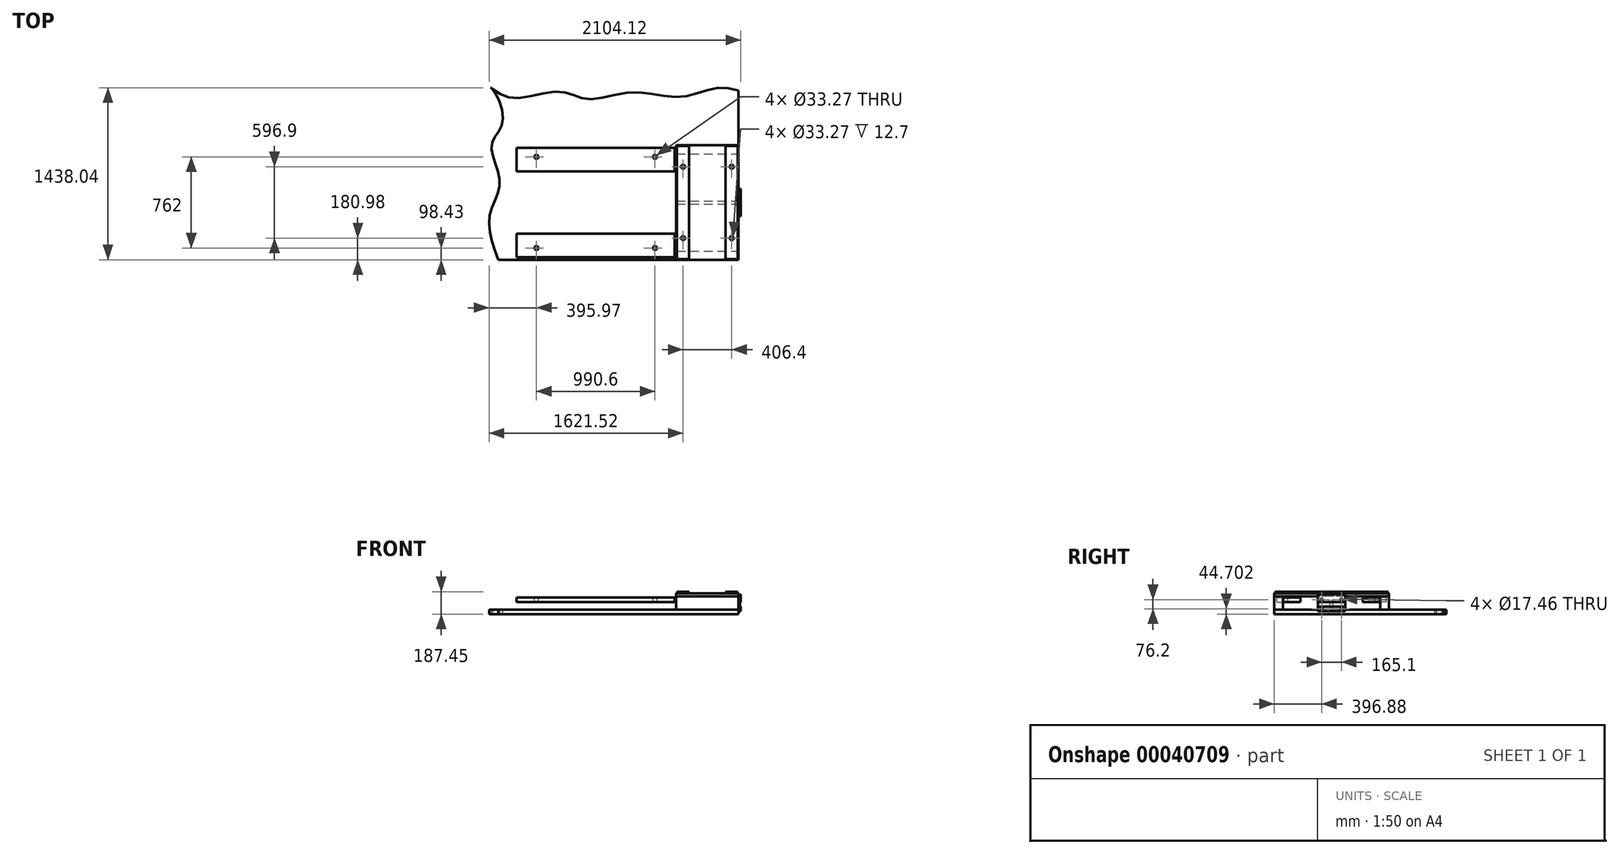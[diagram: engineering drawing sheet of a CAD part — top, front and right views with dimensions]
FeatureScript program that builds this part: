
annotation { "Feature Type Name" : "Feature", "Feature Type Description" : "" }
export const myFeature = defineFeature(function(context is Context, id is Id, definition is map)
    precondition{}
    {
        {
            var Q0;
            Q0=qCreatedBy(makeId("Top.planeOp"),FACE);
            var sketch = newSketch(context, id + "F0", { "sketchPlane" : qUnion([Q0])});
            skLineSegment(sketch, "E0.rect.bottom", {"start": v(-260.35, 479.43) * mm, "end": v(260.35, 479.43) * mm});
            skLineSegment(sketch, "E0.rect.top", {"start": v(-260.35, -479.43) * mm, "end": v(260.35, -479.43) * mm});
            skLineSegment(sketch, "E0.rect.left", {"start": v(-260.35, 479.43) * mm, "end": v(-260.35, -479.43) * mm});
            skLineSegment(sketch, "E0.rect.right", {"start": v(260.35, 479.43) * mm, "end": v(260.35, -479.43) * mm});
            skPoint(sketch, "E0.rect.middle", {"position": v(0, 0) * mm});
            skSolve(sketch);
        }
        {
            var Q0;
            Q0 = qSketchRegion(id + "F0", true);
            extrude(context, id + "F1", {"entities" : qUnion([Q0]), "oppositeDirection" : true, "depth" : 25.4 * mm});
        }
        {
            var Q0;
            Q0=makeQuery(id+"F1.opExtrude","CAP_FACE",FACE,{"disambiguationData":[OSD([sQuery(id+"F0.wireOp",EDGE,"E0.rect.bottom"),sQuery(id+"F0.wireOp",EDGE,"E0.rect.top"),sQuery(id+"F0.wireOp",EDGE,"E0.rect.left"),sQuery(id+"F0.wireOp",EDGE,"E0.rect.right")])],"isStart":true});
            var sketch = newSketch(context, id + "F2", { "sketchPlane" : qUnion([Q0])});
            skLineSegment(sketch, "E1", {"start": v(0, 479.43) * mm, "end": v(0, -479.43) * mm, "construction": true});
            skLineSegment(sketch, "E2.0", {"start": v(152.4, 479.43) * mm, "end": v(152.4, -479.43) * mm, "construction": true});
            skLineSegment(sketch, "E3.0", {"start": v(254, 479.43) * mm, "end": v(254, -479.43) * mm, "construction": true});
            skLineSegment(sketch, "E4.0", {"start": v(-260.35, 479.43) * mm, "end": v(260.35, 479.43) * mm, "construction": true});
            skLineSegment(sketch, "E5.0", {"start": v(-260.35, 473.08) * mm, "end": v(260.35, 473.08) * mm, "construction": true});
            skLineSegment(sketch, "E6.bottom", {"start": v(152.4, 473.08) * mm, "end": v(254, 473.08) * mm});
            skLineSegment(sketch, "E6.top", {"start": v(152.4, -473.07) * mm, "end": v(254, -473.07) * mm});
            skLineSegment(sketch, "E6.left", {"start": v(152.4, 473.08) * mm, "end": v(152.4, -473.07) * mm});
            skLineSegment(sketch, "E6.right", {"start": v(254, 473.08) * mm, "end": v(254, -473.07) * mm});
            skLineSegment(sketch, "E7.0", {"start": v(203.2, 479.43) * mm, "end": v(203.2, -479.43) * mm, "construction": true});
            skLineSegment(sketch, "E8", {"start": v(-359.3, 0) * mm, "end": v(385.16, 0) * mm, "construction": true});
            skLineSegment(sketch, "E9.0", {"start": v(-359.3, 298.45) * mm, "end": v(385.16, 298.45) * mm, "construction": true});
            skCircle(sketch, "E10", {"center": v(203.2, 298.45) * mm, "radius": 16.64 * mm});
            skCircle(sketch, "E11.MirrorC", {"center": v(203.2, -298.45) * mm, "radius": 16.64 * mm});
            skLineSegment(sketch, "E12.MirrorCS", {"start": v(-254, 479.43) * mm, "end": v(-254, -479.42) * mm});
            skLineSegment(sketch, "E13.MirrorCS", {"start": v(-152.4, 479.43) * mm, "end": v(-152.4, -479.42) * mm});
            skLineSegment(sketch, "E14.MirrorCS", {"start": v(-152.4, -473.07) * mm, "end": v(-254, -473.07) * mm});
            skLineSegment(sketch, "E15.MirrorCS", {"start": v(-152.4, 473.08) * mm, "end": v(-152.4, -473.07) * mm});
            skLineSegment(sketch, "E16.MirrorCS", {"start": v(-254, 473.08) * mm, "end": v(-254, -473.07) * mm});
            skLineSegment(sketch, "E17.MirrorCS", {"start": v(-152.4, 473.08) * mm, "end": v(-254, 473.08) * mm});
            skCircle(sketch, "E18.MirrorC", {"center": v(-203.2, -298.45) * mm, "radius": 16.64 * mm});
            skLineSegment(sketch, "E19.MirrorCS", {"start": v(-203.2, 479.43) * mm, "end": v(-203.2, -479.43) * mm, "construction": true});
            skCircle(sketch, "E20.MirrorC", {"center": v(-203.2, 298.45) * mm, "radius": 16.64 * mm});
            skSolve(sketch);
        }
        {
            var Q0;
            Q0 = qSketchRegion(id + "F2", true);
            extrude(context, id + "F3", {"entities" : qUnion([Q0]), "operationType" : NewBodyOperationType.ADD, "depth" : 12.7 * mm});
        }
        {
            var Q0;
            Q0=makeQuery(id+"F3.opExtrude","CAP_FACE",FACE,{"disambiguationData":[OSD([sQuery(id+"F2.wireOp",EDGE,"E14.MirrorCS"),sQuery(id+"F2.wireOp",EDGE,"E15.MirrorCS"),sQuery(id+"F2.wireOp",EDGE,"E16.MirrorCS"),sQuery(id+"F2.wireOp",EDGE,"E17.MirrorCS"),sQuery(id+"F2.wireOp",EDGE,"E18.MirrorC"),sQuery(id+"F2.wireOp",EDGE,"E20.MirrorC")])],"isStart":false});
            cPlane(context, id + "F4", {"entities" : qUnion([Q0]), "cplaneType" : CPlaneType.OFFSET, "offset" : 47.75 * mm, "oppositeDirection" : true, "width" : 152.4 * mm, "height" : 152.4 * mm});
        }
        {
            var Q0;
            Q0=qCreatedBy(id+"F4.planeOp",FACE);
            var sketch = newSketch(context, id + "F5", { "sketchPlane" : qUnion([Q0])});
            skLineSegment(sketch, "E21", {"start": v(0, 742.56) * mm, "end": v(0, -827.84) * mm, "construction": true});
            skLineSegment(sketch, "E22", {"start": v(458.96, 0) * mm, "end": v(-1901, 0) * mm, "construction": true});
            skLineSegment(sketch, "E23.0", {"start": v(-933.45, 742.56) * mm, "end": v(-933.45, -827.84) * mm, "construction": true});
            skLineSegment(sketch, "E24.0", {"start": v(-273.05, 742.56) * mm, "end": v(-273.05, -827.84) * mm, "construction": true});
            skLineSegment(sketch, "E25.0", {"start": v(-1593.85, 742.56) * mm, "end": v(-1593.85, -827.84) * mm, "construction": true});
            skLineSegment(sketch, "E26.0", {"start": v(458.96, -381) * mm, "end": v(-1901, -381) * mm, "construction": true});
            skLineSegment(sketch, "E27.0", {"start": v(458.96, -457.2) * mm, "end": v(-1901, -457.2) * mm, "construction": true});
            skLineSegment(sketch, "E28.0", {"start": v(458.96, -260.35) * mm, "end": v(-1901, -260.35) * mm, "construction": true});
            skLineSegment(sketch, "E29.bottom", {"start": v(-273.05, -457.2) * mm, "end": v(-1593.85, -457.2) * mm});
            skLineSegment(sketch, "E29.top", {"start": v(-273.05, -260.35) * mm, "end": v(-1593.85, -260.35) * mm});
            skLineSegment(sketch, "E29.left", {"start": v(-273.05, -457.2) * mm, "end": v(-273.05, -260.35) * mm});
            skLineSegment(sketch, "E29.right", {"start": v(-1593.85, -457.2) * mm, "end": v(-1593.85, -260.35) * mm});
            skLineSegment(sketch, "E30.0", {"start": v(-1428.75, 742.56) * mm, "end": v(-1428.75, -827.84) * mm, "construction": true});
            skCircle(sketch, "E31", {"center": v(-1428.75, -381) * mm, "radius": 16.64 * mm});
            skCircle(sketch, "E32.MirrorC", {"center": v(-438.15, -381) * mm, "radius": 16.64 * mm});
            skCircle(sketch, "E33.MirrorC", {"center": v(-438.15, 381) * mm, "radius": 16.64 * mm});
            skCircle(sketch, "E34.MirrorC", {"center": v(-1428.75, 381) * mm, "radius": 16.64 * mm});
            skLineSegment(sketch, "E35.MirrorCS", {"start": v(-273.05, 457.2) * mm, "end": v(-273.05, 260.35) * mm});
            skLineSegment(sketch, "E36.MirrorCS", {"start": v(-273.05, 260.35) * mm, "end": v(-1593.85, 260.35) * mm});
            skLineSegment(sketch, "E37.MirrorCS", {"start": v(-273.05, 457.2) * mm, "end": v(-1593.85, 457.2) * mm});
            skLineSegment(sketch, "E38.MirrorCS", {"start": v(-1593.85, 457.2) * mm, "end": v(-1593.85, 260.35) * mm});
            skSolve(sketch);
        }
        {
            var Q0;
            Q0 = qSketchRegion(id + "F5", true);
            extrude(context, id + "F6", {"entities" : qUnion([Q0]), "oppositeDirection" : true, "depth" : 38.1 * mm});
        }
        {
            var Q0;
            Q0=makeQuery(id+"F3.opExtrude","CAP_FACE",FACE,{"disambiguationData":[OSD([sQuery(id+"F2.wireOp",EDGE,"E14.MirrorCS"),sQuery(id+"F2.wireOp",EDGE,"E15.MirrorCS"),sQuery(id+"F2.wireOp",EDGE,"E16.MirrorCS"),sQuery(id+"F2.wireOp",EDGE,"E17.MirrorCS"),sQuery(id+"F2.wireOp",EDGE,"E18.MirrorC"),sQuery(id+"F2.wireOp",EDGE,"E20.MirrorC")])],"isStart":false});
            cPlane(context, id + "F7", {"entities" : qUnion([Q0]), "cplaneType" : CPlaneType.OFFSET, "offset" : 149.35 * mm, "oppositeDirection" : true, "width" : 152.4 * mm, "height" : 152.4 * mm});
        }
        {
            var Q0;
            Q0=qCreatedBy(id+"F7.planeOp",FACE);
            var sketch = newSketch(context, id + "F8", { "sketchPlane" : qUnion([Q0])});
            skLineSegment(sketch, "E39.0", {"start": v(260.35, 936.4) * mm, "end": v(260.35, -479.43) * mm});
            skLineSegment(sketch, "E40.0", {"start": v(-1746.27, -479.43) * mm, "end": v(260.35, -479.43) * mm});
            skLineSegment(sketch, "E41.0", {"start": v(174.5, 479.43) * mm, "end": v(174.5, -479.43) * mm});
            skFitSpline(sketch, "E42", {"points": [v(-1705.26, -578.14) * mm, v(-1821.37, -125.3) * mm, v(-1734.28, 173.68) * mm, v(-1803.95, 478.47) * mm, v(-1708.16, 690.38) * mm, v(-1801.05, 954.53) * mm, v(-1809.76, 957.43) * mm, v(-1809.76, 954.53) * mm], "startDerivative": vector(-880.14, 2085.32) * mm, "endDerivative": vector(39.47, -182.23) * mm});
            skFitSpline(sketch, "E43", {"points": [v(-1809.76, 957.43) * mm, v(-1612.37, 873.25) * mm, v(-1226.3, 925.5) * mm, v(-1008.59, 864.54) * mm, v(-625.42, 919.7) * mm, v(-224.83, 881.96) * mm, v(94.47, 957.43) * mm, v(390.56, 890.67) * mm], "startDerivative": vector(1449.72, -1036.33) * mm, "endDerivative": vector(2114.68, -806.7) * mm});
            skPoint(sketch, "E44.orphan", {"position": v(-260.35, -479.43) * mm});
            skPoint(sketch, "E45.orphan", {"position": v(260.35, 479.43) * mm});
            skSolve(sketch);
        }
        {
            var Q0;
            Q0 = qSketchRegion(id + "F8", true);
            extrude(context, id + "F9", {"entities" : qUnion([Q0]), "oppositeDirection" : true, "depth" : 38.1 * mm});
        }
        {
            var Q0;
            Q0=makeQuery(id+"F1.opExtrude","CAP_FACE",FACE,{"disambiguationData":[OSD([sQuery(id+"F0.wireOp",EDGE,"E0.rect.bottom"),sQuery(id+"F0.wireOp",EDGE,"E0.rect.top"),sQuery(id+"F0.wireOp",EDGE,"E0.rect.left"),sQuery(id+"F0.wireOp",EDGE,"E0.rect.right")])],"isStart":false});
            var sketch = newSketch(context, id + "F10", { "sketchPlane" : qUnion([Q0])});
            skLineSegment(sketch, "E46.0", {"start": v(-260.35, -479.43) * mm, "end": v(-260.35, -406.4) * mm});
            skLineSegment(sketch, "E47.0", {"start": v(-1746.27, 479.43) * mm, "end": v(260.35, 479.43) * mm});
            skLineSegment(sketch, "E48.0", {"start": v(260.35, -936.4) * mm, "end": v(260.35, -406.4) * mm});
            skLineSegment(sketch, "E49.0", {"start": v(-260.35, -479.43) * mm, "end": v(260.35, -479.43) * mm});
            skLineSegment(sketch, "E50", {"start": v(398.75, 0) * mm, "end": v(-463.38, 0) * mm, "construction": true});
            skPoint(sketch, "E50.startSnap0", {"position": v(260.35, 0) * mm});
            skPoint(sketch, "E50.endSnap0", {"position": v(260.35, 0) * mm});
            skLineSegment(sketch, "E51.0", {"start": v(398.75, 406.4) * mm, "end": v(-463.38, 406.4) * mm});
            skLineSegment(sketch, "E52.0", {"start": v(398.75, 12.7) * mm, "end": v(-463.38, 12.7) * mm});
            skLineSegment(sketch, "E53.0", {"start": v(398.75, -12.7) * mm, "end": v(-463.38, -12.7) * mm});
            skLineSegment(sketch, "E54.0", {"start": v(398.75, 431.8) * mm, "end": v(-463.38, 431.8) * mm});
            skLineSegment(sketch, "E55.MirrorCS", {"start": v(398.75, -431.8) * mm, "end": v(-463.38, -431.8) * mm});
            skLineSegment(sketch, "E56.MirrorCS", {"start": v(398.75, -406.4) * mm, "end": v(-463.38, -406.4) * mm});
            skLineSegment(sketch, "E57.trimOffspring", {"start": v(-260.35, 406.4) * mm, "end": v(-260.35, 479.43) * mm});
            skLineSegment(sketch, "E58.trimOffspring", {"start": v(-260.35, -12.7) * mm, "end": v(-260.35, 12.7) * mm});
            skLineSegment(sketch, "E59.trimOffspring", {"start": v(260.35, 406.4) * mm, "end": v(260.35, 479.43) * mm});
            skLineSegment(sketch, "E60.trimOffspring", {"start": v(260.35, -12.7) * mm, "end": v(260.35, 12.7) * mm});
            skSolve(sketch);
        }
        {
            var Q0;
            Q0 = qSketchRegion(id + "F10", true);
            var Q1;
            Q1=makeQuery(id+"F9.opExtrude","SWEPT_BODY",BODY,{"disambiguationData":[OSD([sQuery(id+"F8.wireOp",EDGE,"E39.0"),sQuery(id+"F8.wireOp",EDGE,"E40.0"),sQuery(id+"F8.wireOp",EDGE,"E42"),sQuery(id+"F8.wireOp",EDGE,"E43")])]});
            extrude(context, id + "F11", {"entities" : qUnion([Q0]), "endBound" : BoundingType.UP_TO_BODY, "endBoundEntityBody" : qUnion([Q1]), "depth" : 25.4 * mm});
        }
        {
            var Q0;
            Q0=makeQuery(id+"F1.opExtrude","SWEPT_FACE",FACE,{"disambiguationData":[OSD([sQuery(id+"F0.wireOp",EDGE,"E0.rect.right")])]});
            var sketch = newSketch(context, id + "F12", { "sketchPlane" : qUnion([Q0])});
            skLineSegment(sketch, "E61.0", {"start": v(479.43, 0) * mm, "end": v(-479.42, 0) * mm, "construction": true});
            skLineSegment(sketch, "E62.0", {"start": v(479.43, -9.53) * mm, "end": v(-479.42, -9.53) * mm, "construction": true});
            skLineSegment(sketch, "E63.0", {"start": v(479.43, -149.23) * mm, "end": v(-479.42, -149.23) * mm, "construction": true});
            skLineSegment(sketch, "E64", {"start": v(0, 121.5) * mm, "end": v(0, -214.64) * mm, "construction": true});
            skPoint(sketch, "E64.startSnap0", {"position": v(0, 0) * mm});
            skLineSegment(sketch, "E65.0", {"start": v(-114.3, 121.5) * mm, "end": v(-114.3, -214.64) * mm, "construction": true});
            skLineSegment(sketch, "E66.0", {"start": v(114.3, 121.5) * mm, "end": v(114.3, -214.64) * mm, "construction": true});
            skLineSegment(sketch, "E67.bottom", {"start": v(-114.3, -9.52) * mm, "end": v(114.3, -9.52) * mm});
            skLineSegment(sketch, "E67.top", {"start": v(-114.3, -149.23) * mm, "end": v(114.3, -149.23) * mm});
            skLineSegment(sketch, "E67.left", {"start": v(-114.3, -9.53) * mm, "end": v(-114.3, -149.23) * mm});
            skLineSegment(sketch, "E67.right", {"start": v(114.3, -9.53) * mm, "end": v(114.3, -149.23) * mm});
            skSolve(sketch);
        }
        {
            var Q0;
            Q0 = qSketchRegion(id + "F12", true);
            extrude(context, id + "F13", {"entities" : qUnion([Q0]), "depth" : 19.05 * mm});
        }
        {
            var Q0;
            Q0=makeQuery(id+"F13.opExtrude","SWEPT_FACE",FACE,{"disambiguationData":[OSD([sQuery(id+"F12.wireOp",EDGE,"E67.left")])]});
            var sketch = newSketch(context, id + "F14", { "sketchPlane" : qUnion([Q0])});
            skLineSegment(sketch, "E68.0", {"start": v(152.4, -73.15) * mm, "end": v(254, -73.15) * mm, "construction": true});
            skLineSegment(sketch, "E69.0", {"start": v(152.4, -111.25) * mm, "end": v(254, -111.25) * mm, "construction": true});
            skLineSegment(sketch, "E70.0", {"start": v(279.4, -73.15) * mm, "end": v(279.4, -111.25) * mm});
            skLineSegment(sketch, "E71.0", {"start": v(273.05, -73.15) * mm, "end": v(273.05, -111.25) * mm});
            skLineSegment(sketch, "E72", {"start": v(273.05, -73.15) * mm, "end": v(279.4, -73.15) * mm});
            skLineSegment(sketch, "E73", {"start": v(273.05, -111.25) * mm, "end": v(279.4, -111.25) * mm});
            skPoint(sketch, "E74.orphan", {"position": v(279.4, -9.53) * mm});
            skPoint(sketch, "E75.orphan", {"position": v(279.4, -149.23) * mm});
            skSolve(sketch);
        }
        {
            var Q0;
            Q0 = qSketchRegion(id + "F14", true);
            extrude(context, id + "F15", {"entities" : qUnion([Q0]), "operationType" : NewBodyOperationType.REMOVE, "endBound" : BoundingType.THROUGH_ALL, "oppositeDirection" : true, "depth" : 25.4 * mm});
        }
        {
            var Q0;
            {var subQ0=sQuery(id+"F12.wireOp",EDGE,"E67.bottom");var subQ1=sQuery(id+"F12.wireOp",EDGE,"E67.left");var subQ2=sQuery(id+"F12.wireOp",EDGE,"E67.right");Q0=makeQuery(id+"F15.boolean.opBoolean","SPLIT",FACE,{"disambiguationData":[TD([makeQuery(id+"F13.opExtrude","SWEPT_FACE",FACE,{"disambiguationData":[OSD([subQ0])]})])],"derivedFrom":makeQuery(id+"F13.opExtrude","CAP_FACE",FACE,{"disambiguationData":[OSD([subQ0,sQuery(id+"F12.wireOp",EDGE,"E67.top"),subQ1,subQ2])],"isStart":false})});}
            var sketch = newSketch(context, id + "F16", { "sketchPlane" : qUnion([Q0])});
            skLineSegment(sketch, "E76.0", {"start": v(473.08, -53.85) * mm, "end": v(-473.07, -53.85) * mm, "construction": true});
            skLineSegment(sketch, "E77.0", {"start": v(473.08, -130.05) * mm, "end": v(-473.07, -130.05) * mm, "construction": true});
            skLineSegment(sketch, "E78", {"start": v(0, 81.72) * mm, "end": v(0, -157.6) * mm, "construction": true});
            skLineSegment(sketch, "E79.0", {"start": v(-82.55, 81.72) * mm, "end": v(-82.55, -157.6) * mm, "construction": true});
            skCircle(sketch, "E80", {"center": v(-82.55, -53.85) * mm, "radius": 8.73 * mm});
            skCircle(sketch, "E81", {"center": v(-82.55, -130.05) * mm, "radius": 8.73 * mm});
            skLineSegment(sketch, "E82.0", {"start": v(-114.3, -9.52) * mm, "end": v(114.3, -9.52) * mm, "construction": true});
            skLineSegment(sketch, "E83.0", {"start": v(-114.3, -149.23) * mm, "end": v(114.3, -149.23) * mm, "construction": true});
            skCircle(sketch, "E84.MirrorC", {"center": v(82.55, -53.85) * mm, "radius": 8.73 * mm});
            skCircle(sketch, "E85.MirrorC", {"center": v(82.55, -130.05) * mm, "radius": 8.73 * mm});
            skSolve(sketch);
        }
        {
            var Q0;
            Q0 = qSketchRegion(id + "F16", true);
            extrude(context, id + "F17", {"entities" : qUnion([Q0]), "operationType" : NewBodyOperationType.REMOVE, "oppositeDirection" : true, "depth" : 25.4 * mm});
        }
    });
